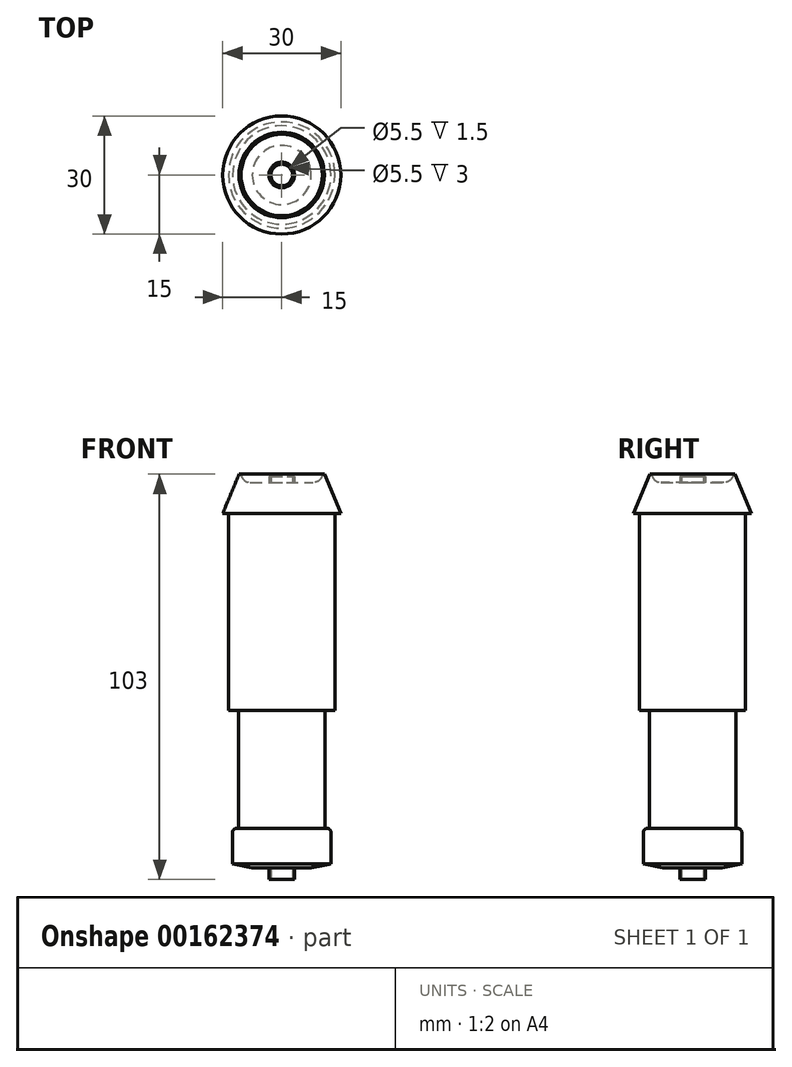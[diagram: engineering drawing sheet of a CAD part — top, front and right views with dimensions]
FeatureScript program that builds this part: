
annotation { "Feature Type Name" : "Feature", "Feature Type Description" : "" }
export const myFeature = defineFeature(function(context is Context, id is Id, definition is map)
    precondition{}
    {
        {
            var Q0;
            Q0=qCreatedBy(makeId("Top.planeOp"),FACE);
            var sketch = newSketch(context, id + "F0", { "sketchPlane" : qUnion([Q0])});
            skCircle(sketch, "E0", {"center": v(0, 0) * mm, "radius": 11 * mm});
            skCircle(sketch, "E1", {"center": v(0, 0) * mm, "radius": 12.5 * mm});
            skCircle(sketch, "E2", {"center": v(0, 0) * mm, "radius": 13.5 * mm});
            skCircle(sketch, "E3", {"center": v(0, 0) * mm, "radius": 15 * mm});
            skSolve(sketch);
        }
        {
            var Q0;
            Q0=makeQuery(id+"F0.imprint","IMPRINT",FACE,{"disambiguationData":[TD([[makeQuery(id+"F0.imprint","IMPRINT",EDGE,{"derivedFrom":sQuery(id+"F0.wireOp",EDGE,"E0")}),1.0]])]});
            extrude(context, id + "F1", {"entities" : qUnion([Q0]), "depth" : 90 * mm});
        }
        {
            var Q0;
            Q0=makeQuery(id+"F0.imprint","IMPRINT",FACE,{"disambiguationData":[TD([[makeQuery(id+"F0.imprint","IMPRINT",EDGE,{"derivedFrom":sQuery(id+"F0.wireOp",EDGE,"E0")}),-1.0]])]});
            extrude(context, id + "F2", {"entities" : qUnion([Q0]), "operationType" : NewBodyOperationType.ADD, "depth" : 10 * mm});
        }
        {
            var Q0;
            Q0=makeQuery(id+"F0.imprint","IMPRINT",FACE,{"disambiguationData":[TD([[makeQuery(id+"F0.imprint","IMPRINT",EDGE,{"derivedFrom":sQuery(id+"F0.wireOp",EDGE,"E1")}),-1.0]])]});
            var Q1;
            Q1=makeQuery(id+"F0.imprint","IMPRINT",FACE,{"disambiguationData":[TD([[makeQuery(id+"F0.imprint","IMPRINT",EDGE,{"derivedFrom":sQuery(id+"F0.wireOp",EDGE,"E0")}),-1.0]])]});
            extrude(context, id + "F3", {"entities" : qUnion([Q0, Q1]), "operationType" : NewBodyOperationType.ADD, "depth" : 90 * mm, "hasSecondDirection" : true, "secondDirectionOppositeDirection" : false, "secondDirectionDepth" : 40 * mm});
        }
        {
            var Q0;
            Q0=qCreatedBy(makeId("Front.planeOp"),FACE);
            var sketch = newSketch(context, id + "F4", { "sketchPlane" : qUnion([Q0])});
            skLineSegment(sketch, "E4", {"start": v(0, 90) * mm, "end": v(-15, 90) * mm});
            skLineSegment(sketch, "E5", {"start": v(-15, 90) * mm, "end": v(-10.84, 100) * mm});
            skLineSegment(sketch, "E6", {"start": v(-8, 97.87) * mm, "end": v(-3.25, 97.87) * mm});
            skLineSegment(sketch, "E7", {"start": v(-2.75, 97.87) * mm, "end": v(-2.75, 99.37) * mm});
            skLineSegment(sketch, "E8", {"start": v(-3.25, 99.37) * mm, "end": v(-2.75, 99.37) * mm});
            skLineSegment(sketch, "E9", {"start": v(-3.25, 99.37) * mm, "end": v(-3.25, 97.87) * mm});
            skLineSegment(sketch, "E10", {"start": v(0, 90) * mm, "end": v(0, 97.87) * mm});
            skLineSegment(sketch, "E11.trimOffspring", {"start": v(-2.75, 97.87) * mm, "end": v(0, 97.87) * mm});
            skLineSegment(sketch, "E12", {"start": v(-8, 97.87) * mm, "end": v(-8, 97.87) * mm});
            skLineSegment(sketch, "E13", {"start": v(-10.84, 100) * mm, "end": v(-10.34, 100) * mm});
            skArc(sketch, "E14", {"start": v(-10.34, 100) * mm, "mid": v(-9.58, 98.48) * mm, "end": v(-8, 97.87) * mm});
            skLineSegment(sketch, "E15", {"start": v(-3.25, 0) * mm, "end": v(-3.25, -3) * mm});
            skLineSegment(sketch, "E16", {"start": v(-3.25, -3) * mm, "end": v(-2.75, -3) * mm});
            skLineSegment(sketch, "E17", {"start": v(-2.75, -3) * mm, "end": v(-2.75, 0) * mm});
            skLineSegment(sketch, "E18", {"start": v(-2.75, 0) * mm, "end": v(-3.25, 0) * mm});
            skSolve(sketch);
        }
        {
            var Q0;
            Q0 = qSketchRegion(id + "F4", true);
            var Q1;
            Q1=sQuery(id+"F4.wireOp",EDGE,"E10");
            revolve(context, id + "F5", {"operationType" : NewBodyOperationType.ADD, "entities" : qUnion([Q0]), "axis" : qUnion([Q1]), "revolveType" : RevolveType.FULL});
        }
        {
            var Q0;
            Q0=makeQuery(id+"F2.opExtrude","CAP_EDGE",EDGE,{"disambiguationData":[OSD([sQuery(id+"F0.wireOp",EDGE,"E1")])],"isStart":false});
            fillet(context, id + "F6", {"entities" : qUnion([Q0]), "radius" : 1 * mm, "tangentPropagation" : true, "allowEdgeOverflow" : false});
        }
        {
            var Q0;
            Q0=makeQuery(id+"F2.opExtrude","CAP_EDGE",EDGE,{"disambiguationData":[OSD([sQuery(id+"F0.wireOp",EDGE,"E1")])],"isStart":true});
            chamfer(context, id + "F7", {"entities" : qUnion([Q0]), "chamferType" : ChamferType.TWO_OFFSETS, "width1" : 1 * mm, "oppositeDirection" : false, "width2" : 5 * mm, "tangentPropagation" : true});
        }
    });
